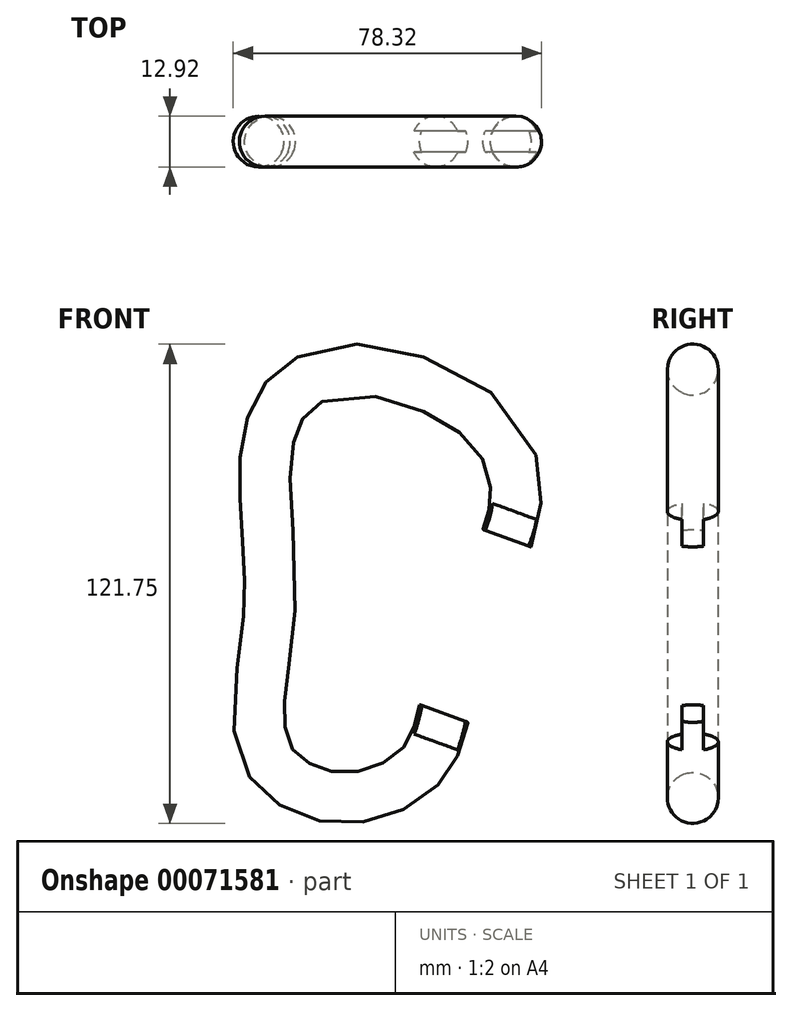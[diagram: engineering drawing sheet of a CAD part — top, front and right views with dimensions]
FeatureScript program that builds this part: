
annotation { "Feature Type Name" : "Feature", "Feature Type Description" : "" }
export const myFeature = defineFeature(function(context is Context, id is Id, definition is map)
    precondition{}
    {
        {
            var Q0;
            Q0=qCreatedBy(makeId("Front.planeOp"),FACE);
            var sketch = newSketch(context, id + "F0", { "sketchPlane" : qUnion([Q0])});
            skFitSpline(sketch, "E0", {"points": [v(21.2, -33.71) * mm, v(15.64, -47.33) * mm, v(-3.68, -55.95) * mm, v(-22.17, -48.03) * mm, v(-25.93, -31.63) * mm, v(-23.15, -5.21) * mm, v(-24.4, 28.15) * mm, v(-18.28, 46.5) * mm, v(1.32, 52.75) * mm, v(34.54, 36.5) * mm, v(39.13, 17.58) * mm, v(37.05, 9.94) * mm], "startDerivative": vector(-41.18, -188.63) * mm, "endDerivative": vector(-44.84, -118.42) * mm});
            skLineSegment(sketch, "E1", {"start": v(37.05, 9.94) * mm, "end": v(21.2, -33.71) * mm, "construction": true});
            skSolve(sketch);
        }
        {
            var Q0;
            Q0=sQuery(id+"F0.wireOp",VERTEX,"E0.end");
            var Q1;
            Q1=sQuery(id+"F0.wireOp",EDGE,"E0");
            cPlane(context, id + "F1", {"entities" : qUnion([Q0, Q1]), "cplaneType" : CPlaneType.CURVE_POINT, "offset" : 150 * mm, "width" : 150 * mm, "height" : 150 * mm});
        }
        {
            var Q0;
            Q0=qCreatedBy(id+"F1.planeOp",FACE);
            var sketch = newSketch(context, id + "F2", { "sketchPlane" : qUnion([Q0])});
            skPoint(sketch, "E2.0", {"position": v(31.13, 0) * mm});
            skCircle(sketch, "E3", {"center": v(31.13, 0) * mm, "radius": 6.46 * mm});
            skSolve(sketch);
        }
        {
            var Q0;
            Q0=makeQuery(id+"F2.imprint","IMPRINT",FACE,{"disambiguationData":[TD([[makeQuery(id+"F2.imprint","IMPRINT",EDGE,{"derivedFrom":sQuery(id+"F2.wireOp",EDGE,"E3")}),1.0]])]});
            var Q1;
            Q1 = qConstructionFilter(qBodyType(qCreatedBy(id + "F0" ,EDGE), BodyType.WIRE), ConstructionObject.NO);
            sweep(context, id + "F3", {"profiles" : qUnion([Q0]), "path" : qUnion([Q1])});
        }
        {
            var Q0;
            Q0=sQuery(id+"F0.wireOp",EDGE,"E1");
            cPlane(context, id + "F4", {"entities" : qUnion([Q0]), "cplaneType" : CPlaneType.LINE_ANGLE, "offset" : 150 * mm, "angle" : 0 * degree, "width" : 150 * mm, "height" : 150 * mm});
        }
        {
            var Q0;
            Q0=qCreatedBy(id+"F4.planeOp",FACE);
            var sketch = newSketch(context, id + "F5", { "sketchPlane" : qUnion([Q0])});
            skEllipse(sketch, "E4.0", {"center": v(0, 21.99) * mm, "majorRadius": 6.46 * mm, "minorRadius": 0.09 * mm, "majorAxis": v(-1, 0)});
            skEllipse(sketch, "E5.0", {"center": v(0, -24.45) * mm, "majorRadius": 6.46 * mm, "minorRadius": 0.86 * mm, "majorAxis": v(-1, 0)});
            skPoint(sketch, "E6", {"position": v(6.46, -24.45) * mm});
            skPoint(sketch, "E7", {"position": v(-6.46, -24.45) * mm});
            skPoint(sketch, "E8", {"position": v(6.46, 21.99) * mm});
            skLineSegment(sketch, "E9.bottom", {"start": v(6.46, 29.11) * mm, "end": v(2.72, 29.11) * mm});
            skLineSegment(sketch, "E9.top", {"start": v(6.46, -32.75) * mm, "end": v(2.72, -32.75) * mm});
            skLineSegment(sketch, "E9.left", {"start": v(6.46, 29.11) * mm, "end": v(6.46, -32.75) * mm});
            skLineSegment(sketch, "E9.right", {"start": v(2.72, 29.11) * mm, "end": v(2.72, -32.75) * mm});
            skLineSegment(sketch, "E10", {"start": v(0, 21.99) * mm, "end": v(0, -9.76) * mm, "construction": true});
            skLineSegment(sketch, "E11.MirrorCS", {"start": v(-2.72, 29.11) * mm, "end": v(-2.72, -32.75) * mm});
            skLineSegment(sketch, "E12.MirrorCS", {"start": v(-6.46, 29.11) * mm, "end": v(-2.72, 29.11) * mm});
            skLineSegment(sketch, "E13.MirrorCS", {"start": v(-6.46, 29.11) * mm, "end": v(-6.46, -32.75) * mm});
            skLineSegment(sketch, "E14.MirrorCS", {"start": v(-6.46, -32.75) * mm, "end": v(-2.72, -32.75) * mm});
            skSolve(sketch);
        }
        {
            var Q0;
            Q0 = qSketchRegion(id + "F5", true);
            extrude(context, id + "F6", {"entities" : qUnion([Q0]), "operationType" : NewBodyOperationType.REMOVE, "endBound" : BoundingType.SYMMETRIC, "oppositeDirection" : true, "depth" : 25 * mm});
        }
    });
